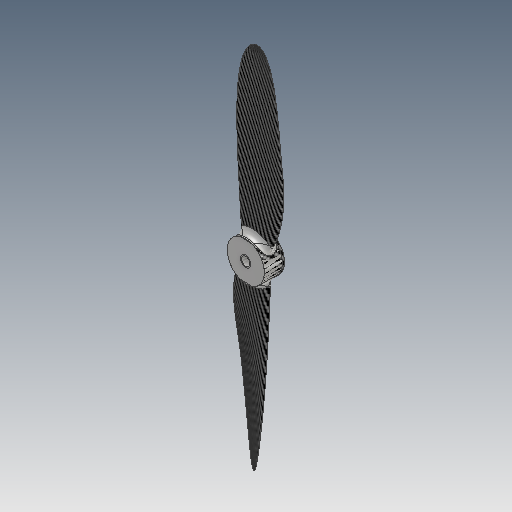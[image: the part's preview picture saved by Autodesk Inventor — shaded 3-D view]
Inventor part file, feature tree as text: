
AUTODESK INVENTOR PART (.ipt)
format: ipt  version: 2018 (Build 220112000, 112)  size: 933,376 bytes
history: native  units: mm
features: other x1, extrude x1, sketch x1, fillet x1
ambient origin geometry x8: Origin, YZ Plane, XZ Plane, XY Plane, X Axis, Y Axis, Z Axis, Center Point
bodies: Volumenkörper1 (feature_tree), Volumenkörper2 (feature_tree)
feature tree (4):
  other  "Flex1"
  extrude  "Extrusion1"  Depth=10.0mm TaperAngle=0.0deg
  sketch  "Skizze1"  dims[d0=5.0mm d1=10.0mm d2=0.0mm]
  fillet  "Fillet8"  [1 undecoded]
note: 1 required parameter value undecoded (feature->parameter linkage not recoverable at this tier; creation-order binding heuristic only, values carry confidence <= 0.55)
